# Revit family: HVAC_Steam-Distribution-Systems_Neptronic_SKD-HD
name_source: partatom
category: Mechanical Equipment
units: mm (PartAtom-declared; Revit-internal decimal feet)

## family parameters
Always vertical = Yes
Classification = None
Cut with Voids When Loaded = No
OmniClass Number = 23.75.70.00
OmniClass Title = HVAC Distribution Devices
Part Type = Normal
Room Calculation Point = No
Round Connector Dimension = Use Diameter
Shared = No
Work Plane-Based = No

## types (1)
- SKD-HD
    Condensate Drain Diameter = 0.50 in
    Default Elevation = 0.00 in
    Description = SKD - Direct Steam Injection Humidifier - Multi-Steam Distribution
    Manufacturer = Neptronic
    Model = SKD-HD
    Product Documentation Link = https://www.neptronic.com
    Product Material = Neptronic - Stainless Steel
    Product Page URL = https://www.neptronic.com
    URL = https://www.neptronic.com
    Version = 1
    z_Tube Min = 2

## geometry (parser evidence)
native form markers: Sweep x9
no freeform markers — native parametric forms only
